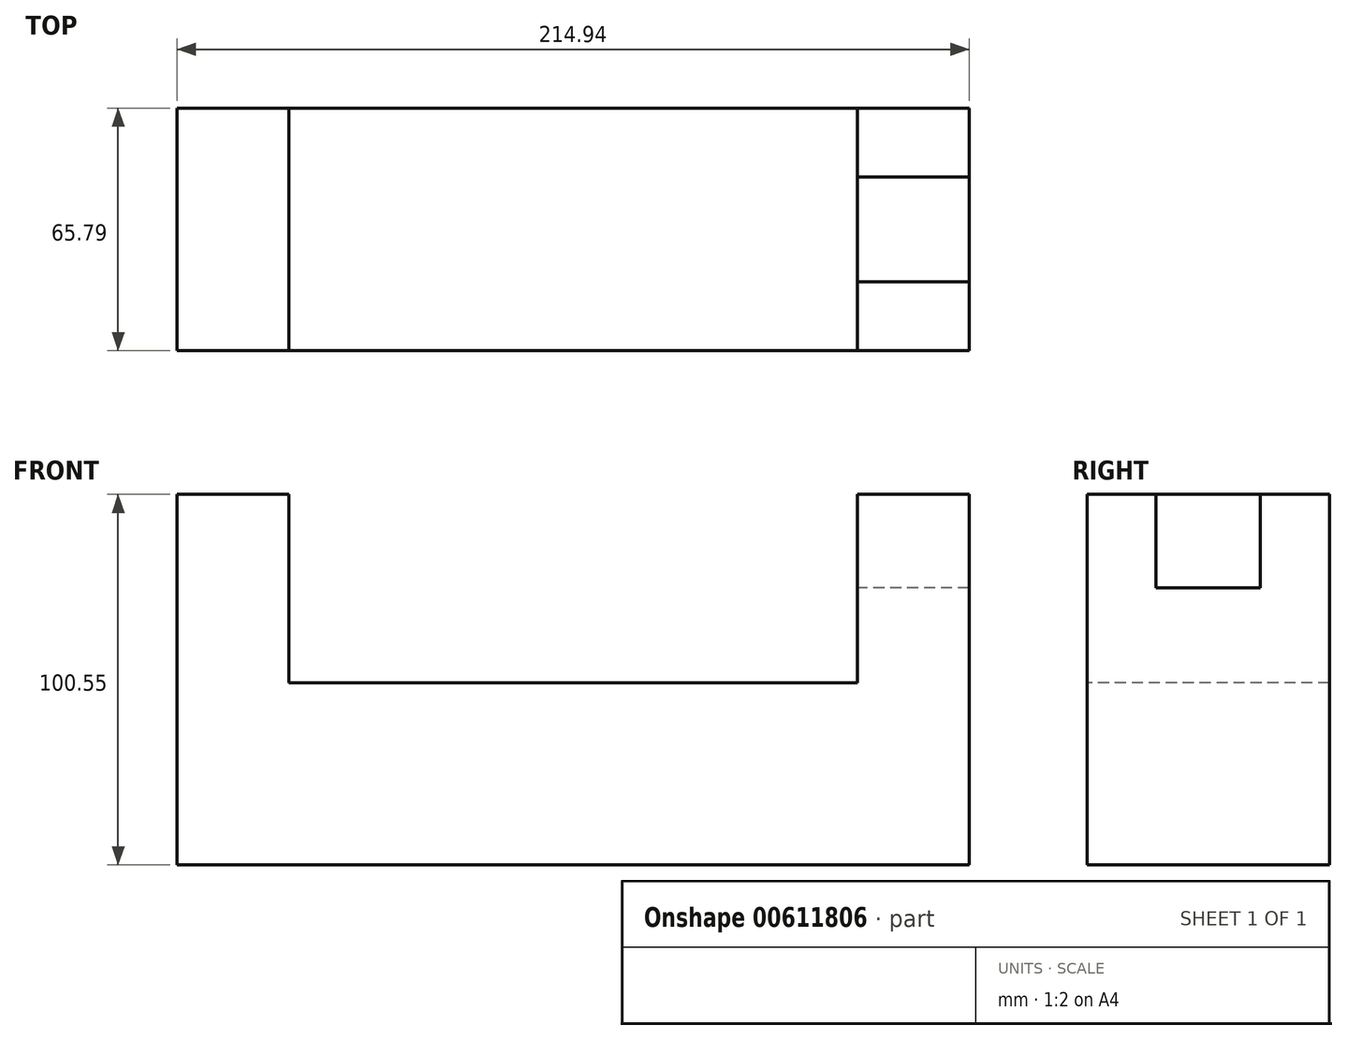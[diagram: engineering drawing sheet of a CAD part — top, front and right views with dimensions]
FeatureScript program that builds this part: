
annotation { "Feature Type Name" : "Feature", "Feature Type Description" : "" }
export const myFeature = defineFeature(function(context is Context, id is Id, definition is map)
    precondition{}
    {
        {
            var Q0;
            Q0=qCreatedBy(makeId("Front.planeOp"),FACE);
            var sketch = newSketch(context, id + "F0", { "sketchPlane" : qUnion([Q0])});
            skLineSegment(sketch, "E0.bottom", {"start": v(-114.68, 76.12) * mm, "end": v(-84.35, 76.12) * mm});
            skLineSegment(sketch, "E0.top", {"start": v(-114.68, -24.43) * mm, "end": v(100.26, -24.43) * mm});
            skLineSegment(sketch, "E0.left", {"start": v(-114.68, 76.12) * mm, "end": v(-114.68, -24.43) * mm});
            skLineSegment(sketch, "E0.right", {"start": v(100.26, 76.12) * mm, "end": v(100.26, -24.43) * mm});
            skLineSegment(sketch, "E1.top", {"start": v(-7.21, 24.98) * mm, "end": v(-84.35, 24.98) * mm});
            skLineSegment(sketch, "E1.right", {"start": v(-84.35, 76.12) * mm, "end": v(-84.35, 24.98) * mm});
            skLineSegment(sketch, "E2.top", {"start": v(-7.21, 24.98) * mm, "end": v(69.92, 24.98) * mm});
            skLineSegment(sketch, "E2.right", {"start": v(69.92, 76.12) * mm, "end": v(69.92, 24.98) * mm});
            skPoint(sketch, "E2.bottom.start.orphan", {"position": v(-7.21, 76.12) * mm});
            skLineSegment(sketch, "E3.trimOffspring", {"start": v(69.92, 76.12) * mm, "end": v(100.26, 76.12) * mm});
            skSolve(sketch);
        }
        {
            var Q0;
            Q0=makeQuery(id+"F0.imprint","IMPRINT",FACE,{"disambiguationData":[TD([[makeQuery(id+"F0.imprint","IMPRINT",EDGE,{"derivedFrom":sQuery(id+"F0.wireOp",EDGE,"E0.bottom")}),-1.0]])]});
            extrude(context, id + "F1", {"entities" : qUnion([Q0]), "oppositeDirection" : true, "depth" : 65.8 * mm, "offsetDistance" : 25.4 * mm});
        }
        {
            var Q0;
            Q0=makeQuery(id+"F1.opExtrude","SWEPT_FACE",FACE,{"disambiguationData":[OSD([sQuery(id+"F0.wireOp",EDGE,"E3.trimOffspring")])]});
            var sketch = newSketch(context, id + "F2", { "sketchPlane" : qUnion([Q0])});
            skLineSegment(sketch, "E4.bottom", {"start": v(100.26, 18.7) * mm, "end": v(69.92, 18.7) * mm});
            skLineSegment(sketch, "E4.top", {"start": v(100.26, 47.08) * mm, "end": v(69.92, 47.08) * mm});
            skLineSegment(sketch, "E4.left", {"start": v(100.26, 18.7) * mm, "end": v(100.26, 47.08) * mm});
            skLineSegment(sketch, "E4.right", {"start": v(69.92, 18.7) * mm, "end": v(69.92, 47.08) * mm});
            skPoint(sketch, "E4.middle", {"position": v(85.1, 32.9) * mm});
            skPoint(sketch, "E5.orphan", {"position": v(100.26, 32.9) * mm});
            skPoint(sketch, "E6.start.orphan", {"position": v(69.92, 32.9) * mm});
            skSolve(sketch);
        }
        {
            var Q0;
            Q0=makeQuery(id+"F2.imprint","IMPRINT",FACE,{"disambiguationData":[TD([[makeQuery(id+"F2.imprint","IMPRINT",EDGE,{"derivedFrom":sQuery(id+"F2.wireOp",EDGE,"E4.bottom")}),-1.0]])]});
            extrude(context, id + "F3", {"entities" : qUnion([Q0]), "operationType" : NewBodyOperationType.REMOVE, "oppositeDirection" : true, "depth" : 25.4 * mm, "offsetDistance" : 25.4 * mm});
        }
    });
